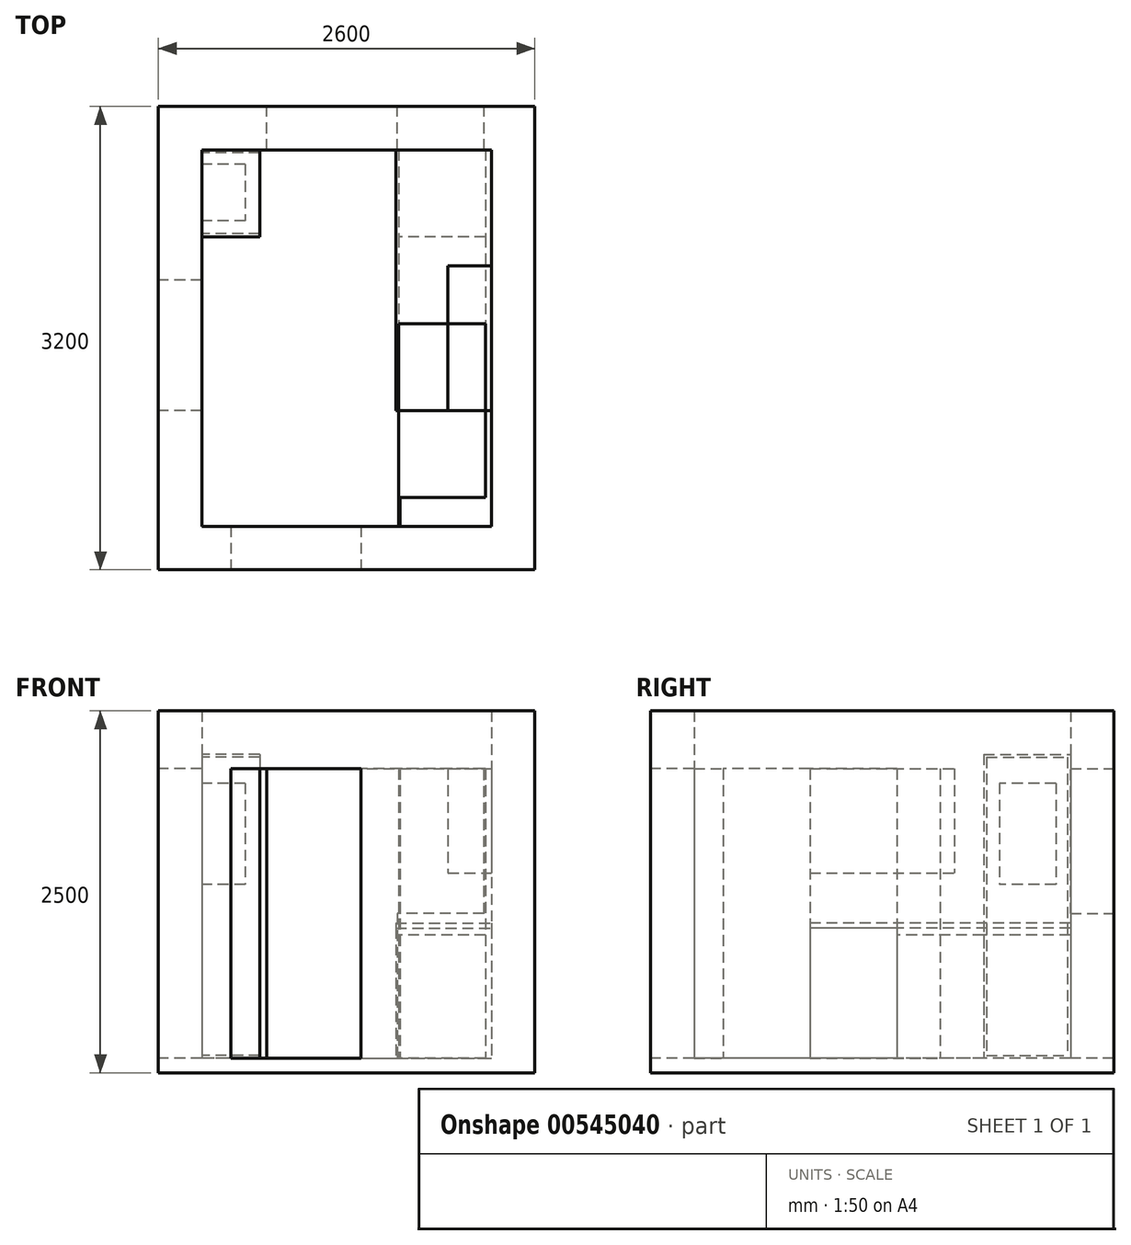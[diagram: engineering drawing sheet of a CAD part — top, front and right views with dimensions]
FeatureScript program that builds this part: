
annotation { "Feature Type Name" : "Feature", "Feature Type Description" : "" }
export const myFeature = defineFeature(function(context is Context, id is Id, definition is map)
    precondition{}
    {
        {
            var Q0;
            Q0=qCreatedBy(makeId("Top.planeOp"),FACE);
            var sketch = newSketch(context, id + "F0", { "sketchPlane" : qUnion([Q0])});
            skLineSegment(sketch, "E0.bottom", {"start": v(-1000, 1300) * mm, "end": v(-550, 1300) * mm});
            skLineSegment(sketch, "E0.top", {"start": v(-1000, -1300) * mm, "end": v(-800, -1300) * mm});
            skLineSegment(sketch, "E0.left", {"start": v(-1000, 1300) * mm, "end": v(-1000, -1300) * mm});
            skLineSegment(sketch, "E0.right", {"start": v(1000, 1300) * mm, "end": v(1000, -1300) * mm});
            skPoint(sketch, "E0.middle", {"position": v(0, 0) * mm});
            skLineSegment(sketch, "E1.bottom", {"start": v(-1300, 1600) * mm, "end": v(-550, 1600) * mm});
            skLineSegment(sketch, "E1.top", {"start": v(-1300, -1600) * mm, "end": v(-800, -1600) * mm});
            skLineSegment(sketch, "E1.left", {"start": v(-1300, 1600) * mm, "end": v(-1300, -1600) * mm});
            skLineSegment(sketch, "E1.right", {"start": v(1300, 1600) * mm, "end": v(1300, -1600) * mm});
            skLineSegment(sketch, "E2", {"start": v(-550, 1600) * mm, "end": v(-550, 1300) * mm});
            skLineSegment(sketch, "E3", {"start": v(350, 1600) * mm, "end": v(350, 1300) * mm});
            skLineSegment(sketch, "E4", {"start": v(100, -1300) * mm, "end": v(100, -1600) * mm});
            skLineSegment(sketch, "E5", {"start": v(-800, -1300) * mm, "end": v(-800, -1600) * mm});
            skLineSegment(sketch, "E6.trimOffspring", {"start": v(350, 1300) * mm, "end": v(1000, 1300) * mm});
            skLineSegment(sketch, "E7.trimOffspring", {"start": v(350, 1600) * mm, "end": v(1300, 1600) * mm});
            skLineSegment(sketch, "E8.trimOffspring", {"start": v(100, -1300) * mm, "end": v(1000, -1300) * mm});
            skLineSegment(sketch, "E9.trimOffspring", {"start": v(100, -1600) * mm, "end": v(1300, -1600) * mm});
            skLineSegment(sketch, "E10", {"start": v(-550, 1600) * mm, "end": v(350, 1600) * mm});
            skLineSegment(sketch, "E11", {"start": v(100, -1600) * mm, "end": v(-800, -1600) * mm});
            skSolve(sketch);
        }
        {
            var Q0;
            Q0=makeQuery(id+"F0.imprint","IMPRINT",FACE,{"disambiguationData":[TD([[makeQuery(id+"F0.imprint","IMPRINT",EDGE,{"derivedFrom":sQuery(id+"F0.wireOp",EDGE,"E0.right")}),1.0]])]});
            var Q1;
            Q1=makeQuery(id+"F0.imprint","IMPRINT",FACE,{"disambiguationData":[TD([[makeQuery(id+"F0.imprint","IMPRINT",EDGE,{"derivedFrom":sQuery(id+"F0.wireOp",EDGE,"E0.bottom")}),1.0]])]});
            extrude(context, id + "F1", {"entities" : qUnion([Q0, Q1]), "depth" : 2400 * mm, "offsetDistance" : 25 * mm});
        }
        {
            var Q0;
            {var subQ3=sQuery(id+"F3.wireOp",EDGE,"E12.right");Q0=makeQuery(id+"F3.imprint","IMPRINT",FACE,{"disambiguationData":[TD([[makeQuery(id+"F3.imprint","IMPRINT",EDGE,{"derivedFrom":subQ3}),-1.0]])]});}
            var Q1;
            Q1=makeQuery(id+"F0.imprint","IMPRINT",FACE,{"disambiguationData":[TD([[makeQuery(id+"F0.imprint","IMPRINT",EDGE,{"derivedFrom":sQuery(id+"F0.wireOp",EDGE,"E0.bottom")}),-1.0]])]});
            var Q2;
            Q2=makeQuery(id+"F0.imprint","IMPRINT",FACE,{"disambiguationData":[TD([[makeQuery(id+"F0.imprint","IMPRINT",EDGE,{"derivedFrom":sQuery(id+"F0.wireOp",EDGE,"E0.bottom")}),1.0]])]});
            var Q3;
            Q3=makeQuery(id+"F0.imprint","IMPRINT",FACE,{"disambiguationData":[TD([[makeQuery(id+"F0.imprint","IMPRINT",EDGE,{"derivedFrom":sQuery(id+"F0.wireOp",EDGE,"E0.right")}),1.0]])]});
            extrude(context, id + "F2", {"entities" : qUnion([Q0, Q1, Q2, Q3]), "operationType" : NewBodyOperationType.ADD, "oppositeDirection" : true, "depth" : 100 * mm, "offsetDistance" : 25 * mm});
        }
        {
            var Q0;
            Q0=makeQuery(id+"F0.imprint","IMPRINT",FACE,{"disambiguationData":[TD([[makeQuery(id+"F0.imprint","IMPRINT",EDGE,{"derivedFrom":sQuery(id+"F0.wireOp",EDGE,"E0.bottom")}),-1.0]])]});
            var sketch = newSketch(context, id + "F3", { "sketchPlane" : qUnion([Q0])});
            skLineSegment(sketch, "E12.bottom", {"start": v(960, 1300) * mm, "end": v(360, 1300) * mm});
            skLineSegment(sketch, "E12.top", {"start": v(960, 700) * mm, "end": v(360, 700) * mm});
            skLineSegment(sketch, "E12.left", {"start": v(960, 1300) * mm, "end": v(960, 700) * mm});
            skLineSegment(sketch, "E12.right", {"start": v(360, 1300) * mm, "end": v(360, 700) * mm});
            skLineSegment(sketch, "E13.top", {"start": v(960, 100) * mm, "end": v(360, 100) * mm});
            skLineSegment(sketch, "E13.left", {"start": v(960, 700) * mm, "end": v(960, 100) * mm});
            skLineSegment(sketch, "E13.right", {"start": v(360, 700) * mm, "end": v(360, 100) * mm});
            skLineSegment(sketch, "E14.top", {"start": v(960, -500) * mm, "end": v(360, -500) * mm});
            skLineSegment(sketch, "E14.left", {"start": v(960, 100) * mm, "end": v(960, -500) * mm});
            skLineSegment(sketch, "E14.right", {"start": v(360, 100) * mm, "end": v(360, -500) * mm});
            skLineSegment(sketch, "E15.top", {"start": v(960, -1100) * mm, "end": v(360, -1100) * mm});
            skLineSegment(sketch, "E15.left", {"start": v(960, -500) * mm, "end": v(960, -1100) * mm});
            skLineSegment(sketch, "E15.right", {"start": v(360, -500) * mm, "end": v(360, -1100) * mm});
            skLineSegment(sketch, "E16", {"start": v(360, -1100) * mm, "end": v(360, -1300) * mm});
            skLineSegment(sketch, "E17", {"start": v(360, -1300) * mm, "end": v(370, -1300) * mm});
            skLineSegment(sketch, "E18", {"start": v(370, -1300) * mm, "end": v(370, -1100) * mm});
            skSolve(sketch);
        }
        {
            var Q0;
            Q0=makeQuery(id+"F3.imprint","IMPRINT",FACE,{"disambiguationData":[TD([[makeQuery(id+"F3.imprint","IMPRINT",EDGE,{"derivedFrom":sQuery(id+"F3.wireOp",EDGE,"E12.bottom")}),-1.0]])]});
            extrude(context, id + "F4", {"entities" : qUnion([Q0]), "depth" : 850 * mm, "offsetDistance" : 25 * mm});
        }
        {
            var Q0;
            Q0=makeQuery(id+"F3.imprint","IMPRINT",FACE,{"disambiguationData":[TD([[makeQuery(id+"F3.imprint","IMPRINT",EDGE,{"derivedFrom":sQuery(id+"F3.wireOp",EDGE,"E12.top")}),1.0]])]});
            extrude(context, id + "F5", {"entities" : qUnion([Q0]), "depth" : 850 * mm, "offsetDistance" : 25 * mm});
        }
        {
            var Q0;
            Q0=makeQuery(id+"F3.imprint","IMPRINT",FACE,{"disambiguationData":[TD([[makeQuery(id+"F3.imprint","IMPRINT",EDGE,{"derivedFrom":sQuery(id+"F3.wireOp",EDGE,"E13.top")}),1.0]])]});
            extrude(context, id + "F6", {"entities" : qUnion([Q0]), "depth" : 2000 * mm, "offsetDistance" : 25 * mm});
        }
        {
            var Q0;
            Q0=makeQuery(id+"F3.imprint","IMPRINT",FACE,{"disambiguationData":[TD([[makeQuery(id+"F3.imprint","IMPRINT",EDGE,{"derivedFrom":sQuery(id+"F3.wireOp",EDGE,"E14.top")}),1.0]])]});
            extrude(context, id + "F7", {"entities" : qUnion([Q0]), "depth" : 2000 * mm, "offsetDistance" : 25 * mm});
        }
        {
            var Q0;
            {var subQ0=sQuery(id+"F3.wireOp",EDGE,"E16");Q0=makeQuery(id+"F3.imprint","IMPRINT",FACE,{"disambiguationData":[TD([[makeQuery(id+"F3.imprint","IMPRINT",EDGE,{"derivedFrom":subQ0}),1.0]])]});}
            extrude(context, id + "F8", {"entities" : qUnion([Q0]), "depth" : 2000 * mm, "offsetDistance" : 25 * mm});
        }
        {
            var Q0;
            {var subQ0=sQuery(id+"F0.wireOp",EDGE,"E7.trimOffspring");var subQ1=sQuery(id+"F0.wireOp",EDGE,"E1.bottom");Q0=makeQuery(id+"F2.boolean.opBoolean","MERGE",FACE,{"derivedFrom":[makeQuery(id+"F1.opExtrude","SWEPT_FACE",FACE,{"disambiguationData":[OSD([subQ1])]}),makeQuery(id+"F1.opExtrude","SWEPT_FACE",FACE,{"disambiguationData":[OSD([subQ0])]}),makeQuery(id+"F2.opExtrude","SWEPT_FACE",FACE,{"disambiguationData":[OSD([subQ1,subQ0,sQuery(id+"F0.wireOp",EDGE,"E10")])]})]});}
            var sketch = newSketch(context, id + "F9", { "sketchPlane" : qUnion([Q0])});
            skLineSegment(sketch, "E19.bottom", {"start": v(-350, 2400) * mm, "end": v(550, 2400) * mm});
            skLineSegment(sketch, "E19.top", {"start": v(-350, 2000) * mm, "end": v(550, 2000) * mm});
            skLineSegment(sketch, "E19.left", {"start": v(-350, 2400) * mm, "end": v(-350, 2000) * mm});
            skLineSegment(sketch, "E19.right", {"start": v(550, 2400) * mm, "end": v(550, 2000) * mm});
            skLineSegment(sketch, "E20.bottom", {"start": v(-350, 2000) * mm, "end": v(-950, 2000) * mm});
            skLineSegment(sketch, "E20.top", {"start": v(-350, 1000) * mm, "end": v(-950, 1000) * mm});
            skLineSegment(sketch, "E20.left", {"start": v(-350, 2000) * mm, "end": v(-350, 1000) * mm});
            skLineSegment(sketch, "E20.right", {"start": v(-950, 2000) * mm, "end": v(-950, 1000) * mm});
            skSolve(sketch);
        }
        {
            var Q0;
            Q0=makeQuery(id+"F9.imprint","IMPRINT",FACE,{"disambiguationData":[TD([[makeQuery(id+"F9.imprint","IMPRINT",EDGE,{"derivedFrom":sQuery(id+"F9.wireOp",EDGE,"E20.bottom")}),1.0]])]});
            extrude(context, id + "F10", {"entities" : qUnion([Q0]), "operationType" : NewBodyOperationType.REMOVE, "endBound" : BoundingType.UP_TO_NEXT, "oppositeDirection" : true, "depth" : 25 * mm, "offsetDistance" : 25 * mm});
        }
        {
            var Q0;
            Q0=makeQuery(id+"F9.imprint","IMPRINT",FACE,{"disambiguationData":[TD([[makeQuery(id+"F9.imprint","IMPRINT",EDGE,{"derivedFrom":sQuery(id+"F9.wireOp",EDGE,"E19.bottom")}),-1.0]])]});
            var Q1;
            Q1=makeQuery(id+"F1.opExtrude","SWEPT_FACE",FACE,{"disambiguationData":[OSD([sQuery(id+"F0.wireOp",EDGE,"E6.trimOffspring")])]});
            extrude(context, id + "F11", {"entities" : qUnion([Q0]), "operationType" : NewBodyOperationType.ADD, "endBound" : BoundingType.UP_TO_SURFACE, "oppositeDirection" : true, "depth" : 25 * mm, "endBoundEntityFace" : qUnion([Q1]), "offsetDistance" : 25 * mm});
        }
        {
            var Q0;
            {var subQ0=sQuery(id+"F0.wireOp",EDGE,"E9.trimOffspring");var subQ1=sQuery(id+"F0.wireOp",EDGE,"E1.top");Q0=makeQuery(id+"F2.boolean.opBoolean","MERGE",FACE,{"derivedFrom":[makeQuery(id+"F1.opExtrude","SWEPT_FACE",FACE,{"disambiguationData":[OSD([subQ1])]}),makeQuery(id+"F1.opExtrude","SWEPT_FACE",FACE,{"disambiguationData":[OSD([subQ0])]}),makeQuery(id+"F2.opExtrude","SWEPT_FACE",FACE,{"disambiguationData":[OSD([subQ1,subQ0,sQuery(id+"F0.wireOp",EDGE,"E11")])]})]});}
            var sketch = newSketch(context, id + "F12", { "sketchPlane" : qUnion([Q0])});
            skLineSegment(sketch, "E21.bottom", {"start": v(100, 2400) * mm, "end": v(-800, 2400) * mm});
            skLineSegment(sketch, "E21.top", {"start": v(100, 2000) * mm, "end": v(-800, 2000) * mm});
            skLineSegment(sketch, "E21.left", {"start": v(100, 2400) * mm, "end": v(100, 2000) * mm});
            skLineSegment(sketch, "E21.right", {"start": v(-800, 2400) * mm, "end": v(-800, 2000) * mm});
            skSolve(sketch);
        }
        {
            var Q0;
            Q0 = qSketchRegion(id + "F12", true);
            var Q1;
            Q1=makeQuery(id+"F1.opExtrude","SWEPT_FACE",FACE,{"disambiguationData":[OSD([sQuery(id+"F0.wireOp",EDGE,"E8.trimOffspring")])]});
            extrude(context, id + "F13", {"entities" : qUnion([Q0]), "operationType" : NewBodyOperationType.ADD, "endBound" : BoundingType.UP_TO_SURFACE, "oppositeDirection" : true, "depth" : 25 * mm, "endBoundEntityFace" : qUnion([Q1]), "offsetDistance" : 25 * mm});
        }
        {
            var Q0;
            {var subQ0=sQuery(id+"F0.wireOp",EDGE,"E1.left");Q0=makeQuery(id+"F2.boolean.opBoolean","MERGE",FACE,{"derivedFrom":[makeQuery(id+"F1.opExtrude","SWEPT_FACE",FACE,{"disambiguationData":[OSD([subQ0])]}),makeQuery(id+"F2.opExtrude","SWEPT_FACE",FACE,{"disambiguationData":[OSD([subQ0])]})]});}
            var sketch = newSketch(context, id + "F14", { "sketchPlane" : qUnion([Q0])});
            skLineSegment(sketch, "E22.bottom", {"start": v(500, 2000) * mm, "end": v(-400, 2000) * mm});
            skLineSegment(sketch, "E22.top", {"start": v(500, -100) * mm, "end": v(-400, -100) * mm});
            skLineSegment(sketch, "E22.left", {"start": v(500, 2000) * mm, "end": v(500, -100) * mm});
            skLineSegment(sketch, "E22.right", {"start": v(-400, 2000) * mm, "end": v(-400, -100) * mm});
            skLineSegment(sketch, "E23", {"start": v(500, 0) * mm, "end": v(-400, 0) * mm});
            skSolve(sketch);
        }
        {
            var Q0;
            {var subQ0=sQuery(id+"F14.wireOp",EDGE,"E22.bottom");Q0=makeQuery(id+"F14.imprint","IMPRINT",FACE,{"disambiguationData":[TD([[makeQuery(id+"F14.imprint","IMPRINT",EDGE,{"derivedFrom":subQ0}),1.0]])]});}
            var Q1;
            Q1=makeQuery(id+"F1.opExtrude","SWEPT_FACE",FACE,{"disambiguationData":[OSD([sQuery(id+"F0.wireOp",EDGE,"E0.left")])]});
            extrude(context, id + "F15", {"entities" : qUnion([Q0]), "operationType" : NewBodyOperationType.REMOVE, "endBound" : BoundingType.UP_TO_SURFACE, "oppositeDirection" : true, "depth" : 25 * mm, "endBoundEntityFace" : qUnion([Q1]), "offsetDistance" : 25 * mm});
        }
        {
            var Q0;
            Q0=makeQuery(id+"F1.opExtrude","SWEPT_FACE",FACE,{"disambiguationData":[OSD([sQuery(id+"F0.wireOp",EDGE,"E0.right")])]});
            var sketch = newSketch(context, id + "F16", { "sketchPlane" : qUnion([Q0])});
            skLineSegment(sketch, "E24", {"start": v(-1300, 890) * mm, "end": v(-100.67, 890) * mm});
            skLineSegment(sketch, "E25", {"start": v(-100.67, 890) * mm, "end": v(-100.67, 860) * mm});
            skLineSegment(sketch, "E26", {"start": v(-100.67, 860) * mm, "end": v(-1300, 860) * mm});
            skLineSegment(sketch, "E27", {"start": v(-1300, 860) * mm, "end": v(-1300, 890) * mm});
            skLineSegment(sketch, "E28.bottom", {"start": v(500, 2000) * mm, "end": v(-500, 2000) * mm});
            skLineSegment(sketch, "E28.top", {"start": v(500, 1280) * mm, "end": v(-500, 1280) * mm});
            skLineSegment(sketch, "E28.left", {"start": v(500, 2000) * mm, "end": v(500, 1280) * mm});
            skLineSegment(sketch, "E28.right", {"start": v(-500, 2000) * mm, "end": v(-500, 1280) * mm});
            skSolve(sketch);
        }
        {
            var Q0;
            Q0=makeQuery(id+"F16.imprint","IMPRINT",FACE,{"disambiguationData":[TD([[makeQuery(id+"F16.imprint","IMPRINT",EDGE,{"derivedFrom":sQuery(id+"F16.wireOp",EDGE,"E28.bottom")}),1.0]])]});
            extrude(context, id + "F17", {"entities" : qUnion([Q0]), "depth" : 300 * mm, "offsetDistance" : 25 * mm});
        }
        {
            var Q0;
            Q0=makeQuery(id+"F1.opExtrude","SWEPT_FACE",FACE,{"disambiguationData":[OSD([sQuery(id+"F0.wireOp",EDGE,"E0.left")])]});
            var sketch = newSketch(context, id + "F18", { "sketchPlane" : qUnion([Q0])});
            skLineSegment(sketch, "E29.bottom", {"start": v(1200, 1900) * mm, "end": v(810, 1900) * mm});
            skLineSegment(sketch, "E29.top", {"start": v(1200, 1200) * mm, "end": v(810, 1200) * mm});
            skLineSegment(sketch, "E29.left", {"start": v(1200, 1900) * mm, "end": v(1200, 1200) * mm});
            skLineSegment(sketch, "E29.right", {"start": v(810, 1900) * mm, "end": v(810, 1200) * mm});
            skSolve(sketch);
        }
        {
            var Q0;
            Q0=makeQuery(id+"F18.imprint","IMPRINT",FACE,{"disambiguationData":[TD([[makeQuery(id+"F18.imprint","IMPRINT",EDGE,{"derivedFrom":sQuery(id+"F18.wireOp",EDGE,"E29.bottom")}),1.0]])]});
            extrude(context, id + "F19", {"entities" : qUnion([Q0]), "depth" : 300 * mm, "offsetDistance" : 25 * mm});
        }
        {
            var Q0;
            Q0=makeQuery(id+"F1.opExtrude","SWEPT_FACE",FACE,{"disambiguationData":[OSD([sQuery(id+"F0.wireOp",EDGE,"E0.left")])]});
            var sketch = newSketch(context, id + "F20", { "sketchPlane" : qUnion([Q0])});
            skLineSegment(sketch, "E30.bottom", {"start": v(700, 2100) * mm, "end": v(1300, 2100) * mm});
            skLineSegment(sketch, "E30.top", {"start": v(700, 0) * mm, "end": v(1300, 0) * mm});
            skLineSegment(sketch, "E30.left", {"start": v(700, 2100) * mm, "end": v(700, 0) * mm});
            skLineSegment(sketch, "E30.right", {"start": v(1300, 2100) * mm, "end": v(1300, 0) * mm});
            skLineSegment(sketch, "E31.bottom", {"start": v(720, 2080) * mm, "end": v(1280, 2080) * mm});
            skLineSegment(sketch, "E31.top", {"start": v(720, 20) * mm, "end": v(1280, 20) * mm});
            skLineSegment(sketch, "E31.left", {"start": v(720, 2080) * mm, "end": v(720, 20) * mm});
            skLineSegment(sketch, "E31.right", {"start": v(1280, 2080) * mm, "end": v(1280, 20) * mm});
            skSolve(sketch);
        }
        {
            var Q0;
            Q0 = qSketchRegion(id + "F20", true);
            extrude(context, id + "F21", {"entities" : qUnion([Q0]), "depth" : 400 * mm, "offsetDistance" : 25 * mm});
        }
        {
            var Q0;
            Q0=makeQuery(id+"F1.opExtrude","SWEPT_FACE",FACE,{"disambiguationData":[OSD([sQuery(id+"F0.wireOp",EDGE,"E0.right")])]});
            var sketch = newSketch(context, id + "F22", { "sketchPlane" : qUnion([Q0])});
            skLineSegment(sketch, "E32.bottom", {"start": v(-100, 900) * mm, "end": v(500, 900) * mm});
            skLineSegment(sketch, "E32.top", {"start": v(-100, 0) * mm, "end": v(500, 0) * mm});
            skLineSegment(sketch, "E32.left", {"start": v(-100, 900) * mm, "end": v(-100, 0) * mm});
            skLineSegment(sketch, "E32.right", {"start": v(500, 900) * mm, "end": v(500, 0) * mm});
            skSolve(sketch);
        }
        {
            var Q0;
            Q0 = qSketchRegion(id + "F22", true);
            extrude(context, id + "F23", {"entities" : qUnion([Q0]), "depth" : 660 * mm, "offsetDistance" : 25 * mm});
        }
        {
            var Q0;
            Q0=makeQuery(id+"F1.opExtrude","SWEPT_FACE",FACE,{"disambiguationData":[OSD([sQuery(id+"F0.wireOp",EDGE,"E0.right")])]});
            var sketch = newSketch(context, id + "F24", { "sketchPlane" : qUnion([Q0])});
            skLineSegment(sketch, "E33.bottom", {"start": v(-1300, 935) * mm, "end": v(500, 935) * mm});
            skLineSegment(sketch, "E33.top", {"start": v(-1300, 900) * mm, "end": v(500, 900) * mm});
            skLineSegment(sketch, "E33.left", {"start": v(-1300, 935) * mm, "end": v(-1300, 900) * mm});
            skLineSegment(sketch, "E33.right", {"start": v(500, 935) * mm, "end": v(500, 900) * mm});
            skSolve(sketch);
        }
        {
            var Q0;
            Q0 = qSketchRegion(id + "F24", true);
            var Q1;
            Q1=makeQuery(id+"F23.opExtrude","CAP_FACE",FACE,{"disambiguationData":[OSD([sQuery(id+"F22.wireOp",EDGE,"E32.bottom"),sQuery(id+"F22.wireOp",EDGE,"E32.top"),sQuery(id+"F22.wireOp",EDGE,"E32.left"),sQuery(id+"F22.wireOp",EDGE,"E32.right")])],"isStart":false});
            extrude(context, id + "F25", {"entities" : qUnion([Q0]), "endBound" : BoundingType.UP_TO_SURFACE, "depth" : 25 * mm, "endBoundEntityFace" : qUnion([Q1]), "offsetDistance" : 25 * mm});
        }
    });
